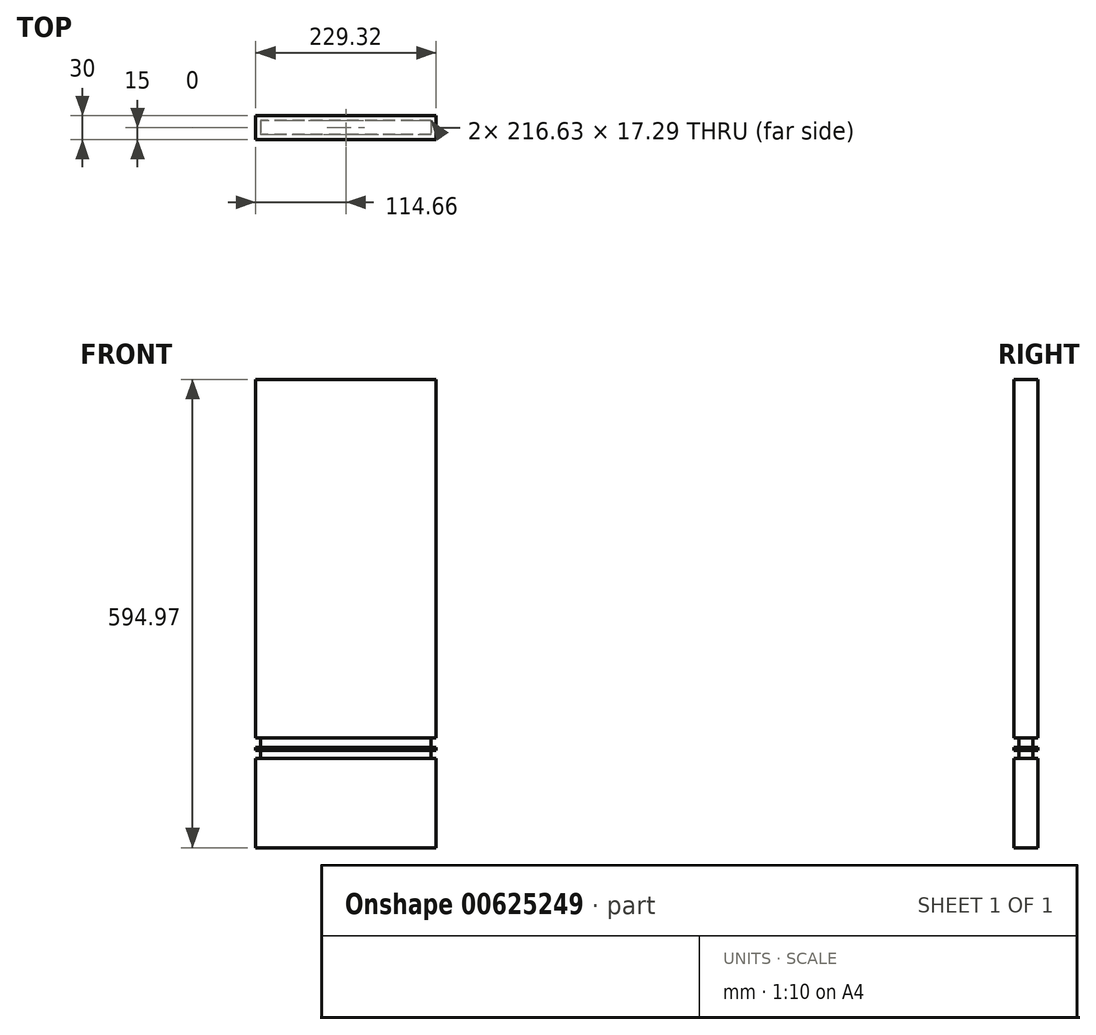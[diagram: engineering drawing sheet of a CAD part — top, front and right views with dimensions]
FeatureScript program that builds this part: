
annotation { "Feature Type Name" : "Feature", "Feature Type Description" : "" }
export const myFeature = defineFeature(function(context is Context, id is Id, definition is map)
    precondition{}
    {
        {
            var Q0;
            Q0=qCreatedBy(makeId("Top.planeOp"),FACE);
            var sketch = newSketch(context, id + "F0", { "sketchPlane" : qUnion([Q0])});
            skLineSegment(sketch, "E0.bottom", {"start": v(114.66, 15) * mm, "end": v(-114.66, 15) * mm});
            skLineSegment(sketch, "E0.top", {"start": v(114.66, -15) * mm, "end": v(-114.66, -15) * mm});
            skLineSegment(sketch, "E0.left", {"start": v(114.66, 15) * mm, "end": v(114.66, -15) * mm});
            skLineSegment(sketch, "E0.right", {"start": v(-114.66, 15) * mm, "end": v(-114.66, -15) * mm});
            skPoint(sketch, "E0.middle", {"position": v(0, 0) * mm});
            skSolve(sketch);
        }
        {
            var Q0;
            Q0=makeQuery(id+"F0.imprint","IMPRINT",FACE,{"disambiguationData":[TD([[makeQuery(id+"F0.imprint","IMPRINT",EDGE,{"derivedFrom":sQuery(id+"F0.wireOp",EDGE,"E0.bottom")}),1.0]])]});
            extrude(context, id + "F1", {"entities" : qUnion([Q0]), "depth" : 113.53 * mm, "offsetDistance" : 25.4 * mm});
        }
        {
            var Q0;
            Q0=makeQuery(id+"F1.opExtrude","CAP_FACE",FACE,{"disambiguationData":[OSD([sQuery(id+"F0.wireOp",EDGE,"E0.bottom"),sQuery(id+"F0.wireOp",EDGE,"E0.top"),sQuery(id+"F0.wireOp",EDGE,"E0.left"),sQuery(id+"F0.wireOp",EDGE,"E0.right")])],"isStart":false});
            var sketch = newSketch(context, id + "F2", { "sketchPlane" : qUnion([Q0])});
            skLineSegment(sketch, "E1.0", {"start": v(108.31, 8.65) * mm, "end": v(-108.31, 8.65) * mm});
            skLineSegment(sketch, "E1.1", {"start": v(108.31, 8.65) * mm, "end": v(108.31, -8.65) * mm});
            skLineSegment(sketch, "E1.2", {"start": v(108.31, -8.65) * mm, "end": v(-108.31, -8.65) * mm});
            skLineSegment(sketch, "E1.3", {"start": v(-108.31, 8.65) * mm, "end": v(-108.31, -8.65) * mm});
            skSolve(sketch);
        }
        {
            var Q0;
            Q0=makeQuery(id+"F2.imprint","IMPRINT",FACE,{"disambiguationData":[TD([[makeQuery(id+"F2.imprint","IMPRINT",EDGE,{"derivedFrom":sQuery(id+"F2.wireOp",EDGE,"E1.0")}),1.0]])]});
            extrude(context, id + "F3", {"entities" : qUnion([Q0]), "operationType" : NewBodyOperationType.ADD, "depth" : 26.34 * mm, "offsetDistance" : 25.4 * mm});
        }
        {
            var Q0;
            Q0=makeQuery(id+"F3.opExtrude","CAP_FACE",FACE,{"disambiguationData":[OSD([sQuery(id+"F2.wireOp",EDGE,"E1.0"),sQuery(id+"F2.wireOp",EDGE,"E1.1"),sQuery(id+"F2.wireOp",EDGE,"E1.2"),sQuery(id+"F2.wireOp",EDGE,"E1.3")])],"isStart":false});
            cPlane(context, id + "F4", {"entities" : qUnion([Q0]), "cplaneType" : CPlaneType.OFFSET, "offset" : 16.48 * mm, "oppositeDirection" : true, "width" : 152.4 * mm, "height" : 152.4 * mm});
        }
        {
            var Q0;
            Q0=qCreatedBy(id+"F4.planeOp",FACE);
            var sketch = newSketch(context, id + "F5", { "sketchPlane" : qUnion([Q0])});
            skLineSegment(sketch, "E2.0", {"start": v(114.66, 15) * mm, "end": v(-114.66, 15) * mm});
            skLineSegment(sketch, "E3.0", {"start": v(114.66, 15) * mm, "end": v(114.66, -15) * mm});
            skLineSegment(sketch, "E4.0", {"start": v(114.66, -15) * mm, "end": v(-114.66, -15) * mm});
            skLineSegment(sketch, "E5.0", {"start": v(-114.66, 15) * mm, "end": v(-114.66, -15) * mm});
            skSolve(sketch);
        }
        {
            var Q0;
            Q0=makeQuery(id+"F5.imprint","IMPRINT",FACE,{"disambiguationData":[TD([[makeQuery(id+"F5.imprint","IMPRINT",EDGE,{"derivedFrom":sQuery(id+"F5.wireOp",EDGE,"E2.0")}),1.0]])]});
            extrude(context, id + "F6", {"entities" : qUnion([Q0]), "operationType" : NewBodyOperationType.ADD, "depth" : 4.4 * mm, "offsetDistance" : 25.4 * mm});
        }
        {
            var Q0;
            Q0=makeQuery(id+"F3.opExtrude","CAP_FACE",FACE,{"disambiguationData":[OSD([sQuery(id+"F2.wireOp",EDGE,"E1.0"),sQuery(id+"F2.wireOp",EDGE,"E1.1"),sQuery(id+"F2.wireOp",EDGE,"E1.2"),sQuery(id+"F2.wireOp",EDGE,"E1.3")])],"isStart":false});
            var sketch = newSketch(context, id + "F7", { "sketchPlane" : qUnion([Q0])});
            skLineSegment(sketch, "E6.0", {"start": v(114.66, 15) * mm, "end": v(-114.66, 15) * mm});
            skLineSegment(sketch, "E7.0", {"start": v(114.66, 15) * mm, "end": v(114.66, -15) * mm});
            skLineSegment(sketch, "E8.0", {"start": v(114.66, -15) * mm, "end": v(-114.66, -15) * mm});
            skPoint(sketch, "E9.0", {"position": v(-114.66, -15) * mm});
            skPoint(sketch, "E10.0", {"position": v(-108.31, -8.65) * mm});
            skLineSegment(sketch, "E11.0", {"start": v(-114.66, 15) * mm, "end": v(-114.66, -15) * mm});
            skSolve(sketch);
        }
        {
            var Q0;
            Q0=makeQuery(id+"F7.imprint","IMPRINT",FACE,{"disambiguationData":[TD([[makeQuery(id+"F7.imprint","IMPRINT",EDGE,{"derivedFrom":sQuery(id+"F7.wireOp",EDGE,"E6.0")}),1.0]])]});
            var Q1;
            Q1=makeQuery(id+"F7.imprint","IMPRINT",FACE,{"disambiguationData":[TD([[makeQuery(id+"F7.imprint","IMPRINT",EDGE,{"derivedFrom":makeQuery(id+"F3.opExtrude","CAP_EDGE",EDGE,{"disambiguationData":[OSD([sQuery(id+"F2.wireOp",EDGE,"E1.0")])],"isStart":false})}),1.0]])]});
            extrude(context, id + "F8", {"entities" : qUnion([Q0, Q1]), "operationType" : NewBodyOperationType.ADD, "depth" : 455.1 * mm, "offsetDistance" : 25.4 * mm});
        }
    });
